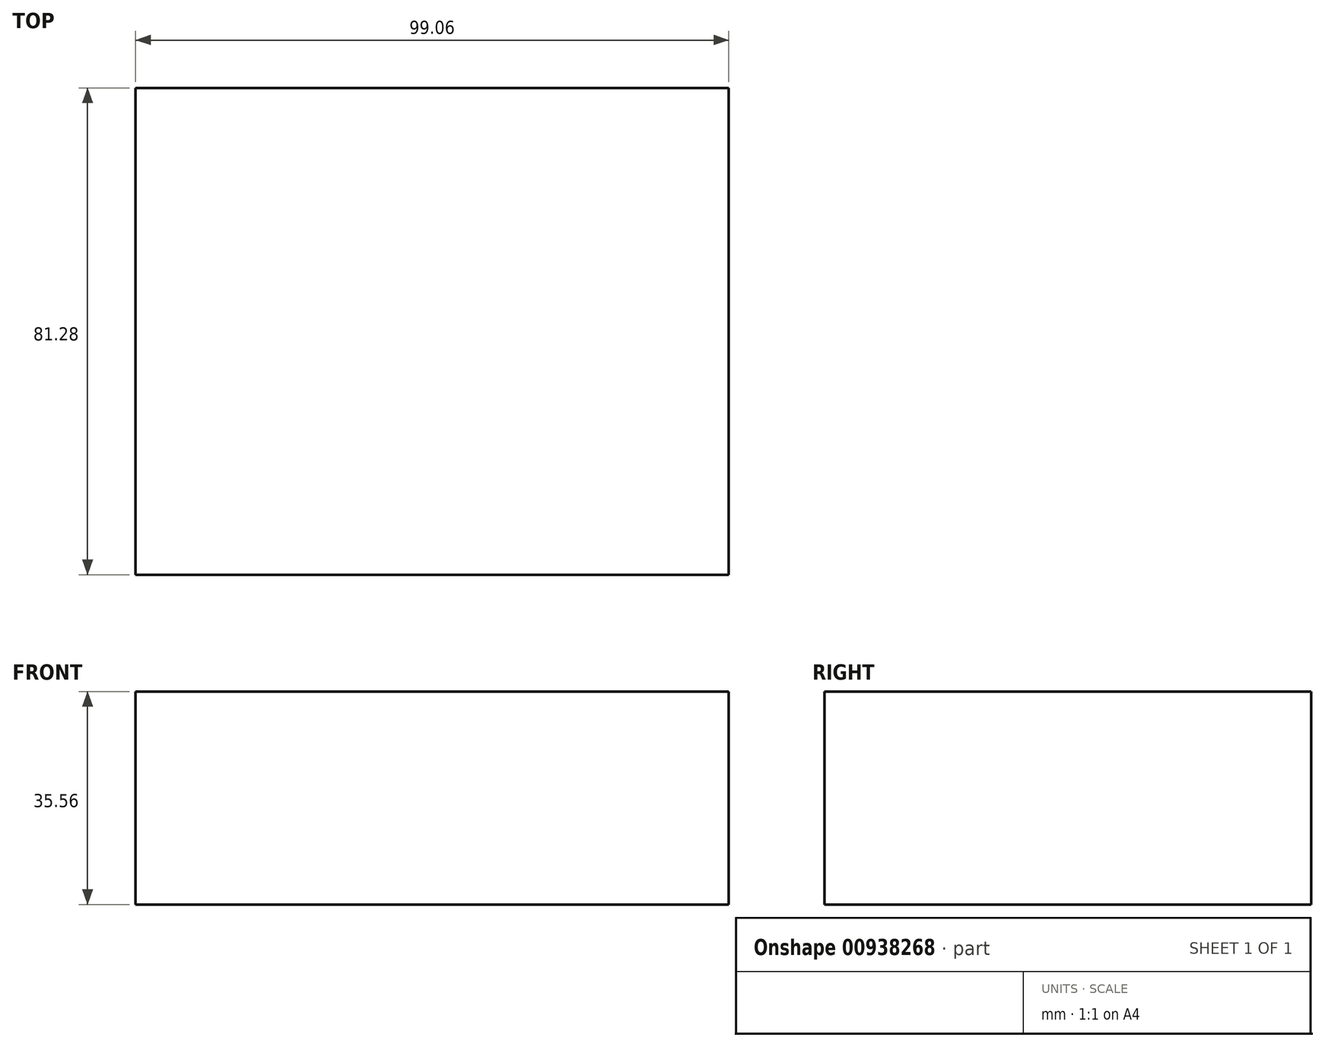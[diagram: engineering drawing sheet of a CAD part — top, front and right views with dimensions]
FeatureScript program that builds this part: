
annotation { "Feature Type Name" : "Feature", "Feature Type Description" : "" }
export const myFeature = defineFeature(function(context is Context, id is Id, definition is map)
    precondition{}
    {
        {
            var Q0;
            Q0=qCreatedBy(makeId("Top.planeOp"),FACE);
            var sketch = newSketch(context, id + "F0", { "sketchPlane" : qUnion([Q0])});
            skLineSegment(sketch, "E0.bottom", {"start": v(44.58, -34.64) * mm, "end": v(-54.48, -34.64) * mm});
            skLineSegment(sketch, "E0.top", {"start": v(44.58, 46.64) * mm, "end": v(-54.48, 46.64) * mm});
            skLineSegment(sketch, "E0.left", {"start": v(44.58, -34.64) * mm, "end": v(44.58, 46.64) * mm});
            skLineSegment(sketch, "E0.right", {"start": v(-54.48, -34.64) * mm, "end": v(-54.48, 46.64) * mm});
            skSolve(sketch);
        }
        {
            var Q0;
            Q0=makeQuery(id+"F0.imprint","IMPRINT",FACE,{"disambiguationData":[TD([[makeQuery(id+"F0.imprint","IMPRINT",EDGE,{"derivedFrom":sQuery(id+"F0.wireOp",EDGE,"E0.bottom")}),-1.0]])]});
            extrude(context, id + "F1", {"entities" : qUnion([Q0]), "depth" : 35.56 * mm, "offsetDistance" : 25.4 * mm});
        }
    });
